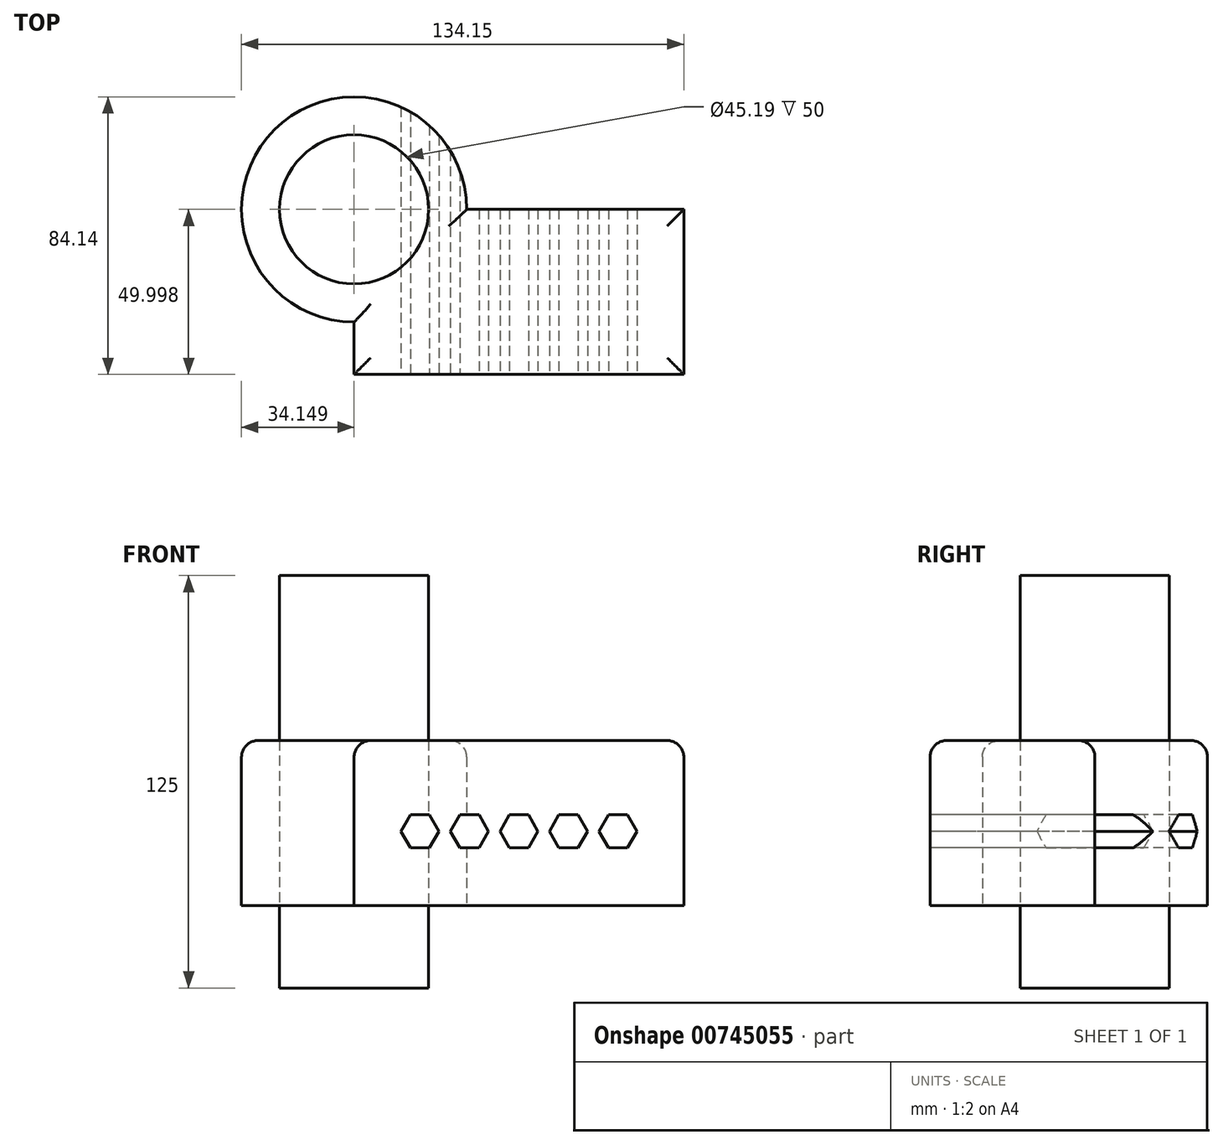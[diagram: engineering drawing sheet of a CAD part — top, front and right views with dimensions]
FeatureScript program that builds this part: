
annotation { "Feature Type Name" : "Feature", "Feature Type Description" : "" }
export const myFeature = defineFeature(function(context is Context, id is Id, definition is map)
    precondition{}
    {
        {
            var Q0;
            Q0=qCreatedBy(makeId("Top.planeOp"),FACE);
            var sketch = newSketch(context, id + "F0", { "sketchPlane" : qUnion([Q0])});
            skLineSegment(sketch, "E0.bottom", {"start": v(-42.54, 22.59) * mm, "end": v(57.46, 22.59) * mm});
            skLineSegment(sketch, "E0.top", {"start": v(-42.54, -27.41) * mm, "end": v(57.46, -27.41) * mm});
            skLineSegment(sketch, "E0.left", {"start": v(-42.54, 22.59) * mm, "end": v(-42.54, -27.41) * mm});
            skLineSegment(sketch, "E0.right", {"start": v(57.46, 22.59) * mm, "end": v(57.46, -27.41) * mm});
            skCircle(sketch, "E1", {"center": v(-42.54, 22.59) * mm, "radius": 34.14 * mm});
            skArc(sketch, "E2", {"start": v(-21.66, 49.6) * mm, "mid": v(15.66, 29.53) * mm, "end": v(57.46, 22.59) * mm});
            skCircle(sketch, "E3", {"center": v(-42.54, 22.59) * mm, "radius": 22.6 * mm});
            skSolve(sketch);
        }
        {
            var Q0;
            {var subQ4=sQuery(id+"F0.wireOp",EDGE,"E0.bottom");var subQ6=sQuery(id+"F0.wireOp",EDGE,"E3");var subQ8=makeQuery(id+"F0.imprint","INTERSECT",VERTEX,{"derivedFrom":[subQ4,subQ6]});Q0=makeQuery(id+"F0.imprint","IMPRINT",FACE,{"disambiguationData":[TD([[makeQuery(id+"F0.imprint","IMPRINT",EDGE,{"disambiguationData":[TD([[subQ8,-1.0]])],"derivedFrom":subQ4}),1.0]])]});}
            var Q1;
            {var subQ1=sQuery(id+"F0.wireOp",EDGE,"E0.top");Q1=makeQuery(id+"F0.imprint","IMPRINT",FACE,{"disambiguationData":[TD([[makeQuery(id+"F0.imprint","IMPRINT",EDGE,{"derivedFrom":subQ1}),1.0]])]});}
            var Q2;
            {var subQ0=sQuery(id+"F0.wireOp",EDGE,"E3");var subQ1=sQuery(id+"F0.wireOp",EDGE,"E0.bottom");var subQ2=makeQuery(id+"F0.imprint","INTERSECT",VERTEX,{"derivedFrom":[subQ1,subQ0]});Q2=makeQuery(id+"F0.imprint","IMPRINT",FACE,{"disambiguationData":[TD([[makeQuery(id+"F0.imprint","IMPRINT",EDGE,{"disambiguationData":[TD([[subQ2,-1.0]])],"derivedFrom":subQ1}),-1.0]])]});}
            var Q3;
            Q3=sQuery(id+"F0.wireOp",EDGE,"E0.top");
            extrude(context, id + "F1", {"entities" : qUnion([Q0, Q1, Q2]), "surfaceEntities" : qUnion([Q3]), "depth" : 50 * mm, "offsetDistance" : 25 * mm});
        }
        {
            var Q0;
            {var subQ0=sQuery(id+"F0.wireOp",EDGE,"E0.left");var subQ1=sQuery(id+"F0.wireOp",EDGE,"E0.bottom");var subQ2=makeQuery(id+"F0.imprint","INTERSECT",VERTEX,{"derivedFrom":[subQ1,subQ0]});Q0=makeQuery(id+"F0.imprint","IMPRINT",FACE,{"disambiguationData":[TD([[makeQuery(id+"F0.imprint","IMPRINT",EDGE,{"disambiguationData":[TD([[subQ2,-1.0]])],"derivedFrom":subQ1}),1.0]])]});}
            var Q1;
            {var subQ0=sQuery(id+"F0.wireOp",EDGE,"E0.left");var subQ1=sQuery(id+"F0.wireOp",EDGE,"E0.bottom");var subQ2=makeQuery(id+"F0.imprint","INTERSECT",VERTEX,{"derivedFrom":[subQ1,subQ0]});Q1=makeQuery(id+"F0.imprint","IMPRINT",FACE,{"disambiguationData":[TD([[makeQuery(id+"F0.imprint","IMPRINT",EDGE,{"disambiguationData":[TD([[subQ2,-1.0]])],"derivedFrom":subQ1}),-1.0]])]});}
            extrude(context, id + "F2", {"entities" : qUnion([Q0, Q1]), "depth" : 100 * mm, "offsetDistance" : 25 * mm, "hasSecondDirection" : true, "secondDirectionOppositeDirection" : true, "secondDirectionDepth" : 25 * mm});
        }
        {
            var Q0;
            Q0=makeQuery(id+"F1.opExtrude","CAP_EDGE",EDGE,{"disambiguationData":[OSD([sQuery(id+"F0.wireOp",EDGE,"E0.top")])],"isStart":false});
            var Q1;
            Q1=makeQuery(id+"F1.opExtrude","CAP_EDGE",EDGE,{"disambiguationData":[OSD([sQuery(id+"F0.wireOp",EDGE,"E0.left")])],"isStart":false});
            var Q2;
            Q2=makeQuery(id+"F1.opExtrude","CAP_EDGE",EDGE,{"disambiguationData":[OSD([sQuery(id+"F0.wireOp",EDGE,"E1")])],"isStart":false});
            var Q3;
            Q3=makeQuery(id+"F1.opExtrude","CAP_EDGE",EDGE,{"disambiguationData":[OSD([sQuery(id+"F0.wireOp",EDGE,"E0.bottom")])],"isStart":false});
            var Q4;
            Q4=makeQuery(id+"F1.opExtrude","CAP_EDGE",EDGE,{"disambiguationData":[OSD([sQuery(id+"F0.wireOp",EDGE,"E0.right")])],"isStart":false});
            fillet(context, id + "F3", {"entities" : qUnion([Q0, Q1, Q2, Q3, Q4]), "radius" : 5 * mm, "tangentPropagation" : true, "allowEdgeOverflow" : false});
        }
        {
            var Q0;
            Q0=makeQuery(id+"F1.opExtrude","SWEPT_FACE",FACE,{"disambiguationData":[OSD([sQuery(id+"F0.wireOp",EDGE,"E0.top")])]});
            var sketch = newSketch(context, id + "F4", { "sketchPlane" : qUnion([Q0])});
            skCircle(sketch, "E4.cCircle", {"center": v(-22.54, 22.5) * mm, "radius": 5 * mm, "construction": true});
            skPoint(sketch, "E4.cCircle.centerSnap0", {"position": v(-42.54, 22.5) * mm});
            skLineSegment(sketch, "E4.0", {"start": v(-16.77, 22.5) * mm, "end": v(-19.65, 17.5) * mm});
            skLineSegment(sketch, "E4.1", {"start": v(-19.65, 17.5) * mm, "end": v(-25.43, 17.5) * mm});
            skLineSegment(sketch, "E4.2", {"start": v(-25.43, 17.5) * mm, "end": v(-28.31, 22.5) * mm});
            skLineSegment(sketch, "E4.3", {"start": v(-28.31, 22.5) * mm, "end": v(-25.43, 27.5) * mm});
            skLineSegment(sketch, "E4.4", {"start": v(-25.43, 27.5) * mm, "end": v(-19.65, 27.5) * mm});
            skLineSegment(sketch, "E4.5", {"start": v(-19.65, 27.5) * mm, "end": v(-16.77, 22.5) * mm});
            skPoint(sketch, "E4.0.midPoint", {"position": v(-18.21, 20) * mm});
            skLineSegment(sketch, "E5.1.0.0", {"start": v(-10.43, 27.5) * mm, "end": v(-4.65, 27.5) * mm});
            skLineSegment(sketch, "E5.1.0.1", {"start": v(-13.31, 22.5) * mm, "end": v(-10.43, 27.5) * mm});
            skLineSegment(sketch, "E5.1.0.2", {"start": v(-10.43, 17.5) * mm, "end": v(-13.31, 22.5) * mm});
            skLineSegment(sketch, "E5.1.0.3", {"start": v(-4.65, 17.5) * mm, "end": v(-10.43, 17.5) * mm});
            skLineSegment(sketch, "E5.1.0.4", {"start": v(-1.77, 22.5) * mm, "end": v(-4.65, 17.5) * mm});
            skCircle(sketch, "E5.1.0.5", {"center": v(-7.54, 22.5) * mm, "radius": 5 * mm, "construction": true});
            skPoint(sketch, "E5.1.0.6", {"position": v(-3.21, 20) * mm});
            skLineSegment(sketch, "E5.1.0.7", {"start": v(-4.65, 27.5) * mm, "end": v(-1.77, 22.5) * mm});
            skLineSegment(sketch, "E5.2.0.0", {"start": v(4.57, 27.5) * mm, "end": v(10.35, 27.5) * mm});
            skLineSegment(sketch, "E5.2.0.1", {"start": v(1.69, 22.5) * mm, "end": v(4.57, 27.5) * mm});
            skLineSegment(sketch, "E5.2.0.2", {"start": v(4.57, 17.5) * mm, "end": v(1.69, 22.5) * mm});
            skLineSegment(sketch, "E5.2.0.3", {"start": v(10.35, 17.5) * mm, "end": v(4.57, 17.5) * mm});
            skLineSegment(sketch, "E5.2.0.4", {"start": v(13.23, 22.5) * mm, "end": v(10.35, 17.5) * mm});
            skCircle(sketch, "E5.2.0.5", {"center": v(7.46, 22.5) * mm, "radius": 5 * mm, "construction": true});
            skPoint(sketch, "E5.2.0.6", {"position": v(11.79, 20) * mm});
            skLineSegment(sketch, "E5.2.0.7", {"start": v(10.35, 27.5) * mm, "end": v(13.23, 22.5) * mm});
            skLineSegment(sketch, "E5.3.0.0", {"start": v(19.57, 27.5) * mm, "end": v(25.35, 27.5) * mm});
            skLineSegment(sketch, "E5.3.0.1", {"start": v(16.69, 22.5) * mm, "end": v(19.57, 27.5) * mm});
            skLineSegment(sketch, "E5.3.0.2", {"start": v(19.57, 17.5) * mm, "end": v(16.69, 22.5) * mm});
            skLineSegment(sketch, "E5.3.0.3", {"start": v(25.35, 17.5) * mm, "end": v(19.57, 17.5) * mm});
            skLineSegment(sketch, "E5.3.0.4", {"start": v(28.23, 22.5) * mm, "end": v(25.35, 17.5) * mm});
            skCircle(sketch, "E5.3.0.5", {"center": v(22.46, 22.5) * mm, "radius": 5 * mm, "construction": true});
            skPoint(sketch, "E5.3.0.6", {"position": v(26.79, 20) * mm});
            skLineSegment(sketch, "E5.3.0.7", {"start": v(25.35, 27.5) * mm, "end": v(28.23, 22.5) * mm});
            skLineSegment(sketch, "E5.4.0.0", {"start": v(34.57, 27.5) * mm, "end": v(40.35, 27.5) * mm});
            skLineSegment(sketch, "E5.4.0.1", {"start": v(31.69, 22.5) * mm, "end": v(34.57, 27.5) * mm});
            skLineSegment(sketch, "E5.4.0.2", {"start": v(34.57, 17.5) * mm, "end": v(31.69, 22.5) * mm});
            skLineSegment(sketch, "E5.4.0.3", {"start": v(40.35, 17.5) * mm, "end": v(34.57, 17.5) * mm});
            skLineSegment(sketch, "E5.4.0.4", {"start": v(43.23, 22.5) * mm, "end": v(40.35, 17.5) * mm});
            skCircle(sketch, "E5.4.0.5", {"center": v(37.46, 22.5) * mm, "radius": 5 * mm, "construction": true});
            skPoint(sketch, "E5.4.0.6", {"position": v(41.79, 20) * mm});
            skLineSegment(sketch, "E5.4.0.7", {"start": v(40.35, 27.5) * mm, "end": v(43.23, 22.5) * mm});
            skLineSegment(sketch, "E5.direction1", {"start": v(-28.31, 22.5) * mm, "end": v(-13.31, 22.5) * mm, "construction": true});
            skSolve(sketch);
        }
        {
            var Q0;
            Q0 = qSketchRegion(id + "F4", true);
            extrude(context, id + "F5", {"entities" : qUnion([Q0]), "operationType" : NewBodyOperationType.REMOVE, "endBound" : BoundingType.THROUGH_ALL, "oppositeDirection" : true, "depth" : 25 * mm, "offsetDistance" : 25 * mm});
        }
    });
